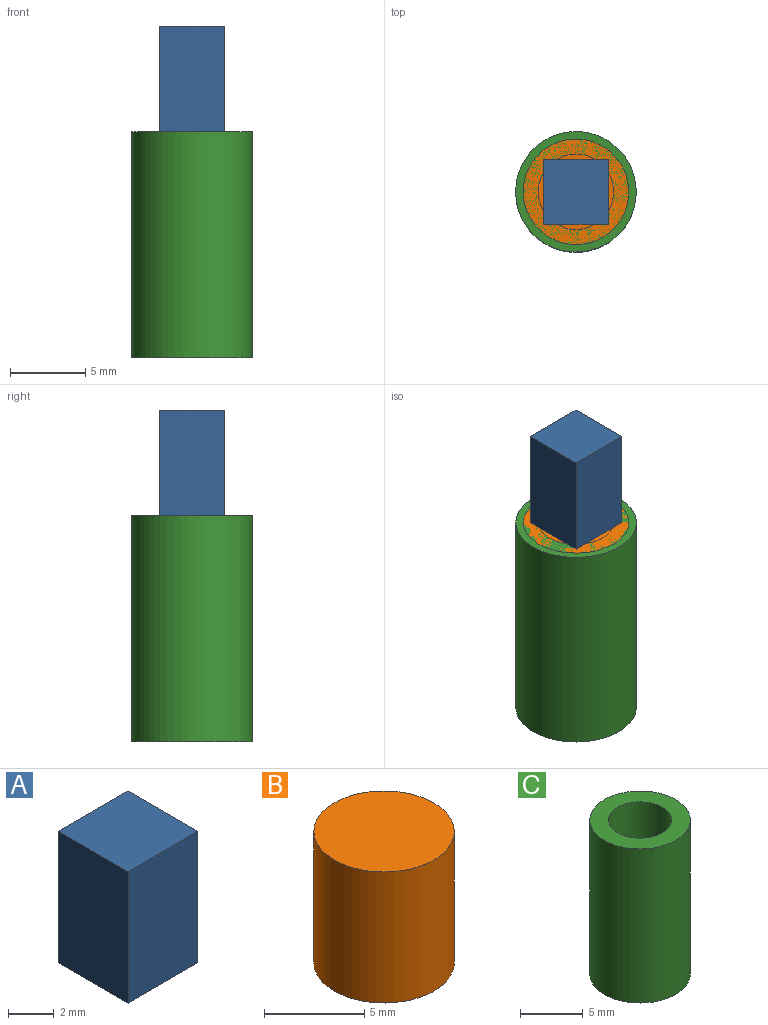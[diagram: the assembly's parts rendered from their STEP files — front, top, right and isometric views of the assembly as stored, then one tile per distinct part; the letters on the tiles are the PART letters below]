
ASSEMBLY  parts=3 mates=2
PART A: 6 faces, bbox 4.3x4.3x7 mm
  f0: plane 7x4.3mm, normal (0,-1,0), area 30.1mm2, adj f1,f3,f4,f5
  f1: plane 7x4.3mm, normal (1,0,0), area 30.1mm2, adj f0,f2,f4,f5
  f2: plane 7x4.3mm, normal (0,1,0), area 30.1mm2, adj f1,f3,f4,f5
  f3: plane 7x4.3mm, normal (-1,0,0), area 30.1mm2, adj f0,f2,f4,f5
  f4: plane 4.3x4.3mm, normal (0,0,1), area 18.5mm2, adj f0,f1,f2,f3
  f5: plane 4.3x4.3mm, normal (0,0,-1), area 18.5mm2, adj f0,f1,f2,f3
PART B: 3 faces, bbox 7x7x8 mm
  f0: cylinder r=3.5mm len=8mm, axis (0,0,-1), area 175.9mm2, adj f1,f2
  f1: plane 7x7mm, normal (0,0,1), area 38.5mm2, adj f0
  f2: plane 7x7mm, normal (0,0,-1), area 38.5mm2, adj f0
PART C: 4 faces, bbox 8x8x15 mm
  f0: cylinder r=2.5mm len=15mm, axis (0,0,-1), area 235.6mm2, adj f2,f3
  f1: cylinder r=4mm len=15mm, axis (0,0,-1), area 377mm2, adj f2,f3
  f2: plane 8x8mm, normal (0,0,1), area 30.6mm2, adj f0,f1
  f3: plane 8x8mm, normal (0,0,-1), area 30.6mm2, adj f0,f1
PLACE A rot(axis=(1,0,0),180deg) t=(4.24,3.49,12.56)mm
PLACE B t=(4.24,3.49,-2.44)mm
PLACE C t=(4.24,3.49,-9.44)mm
MATE fastened C.f0 <-> B.f0  axis (0,0,1) through (4.24,3.49,5.56)mm
MATE fastened A.f4 <-> C.f0  axis (0,0,-1) through (4.24,3.49,5.56)mm
